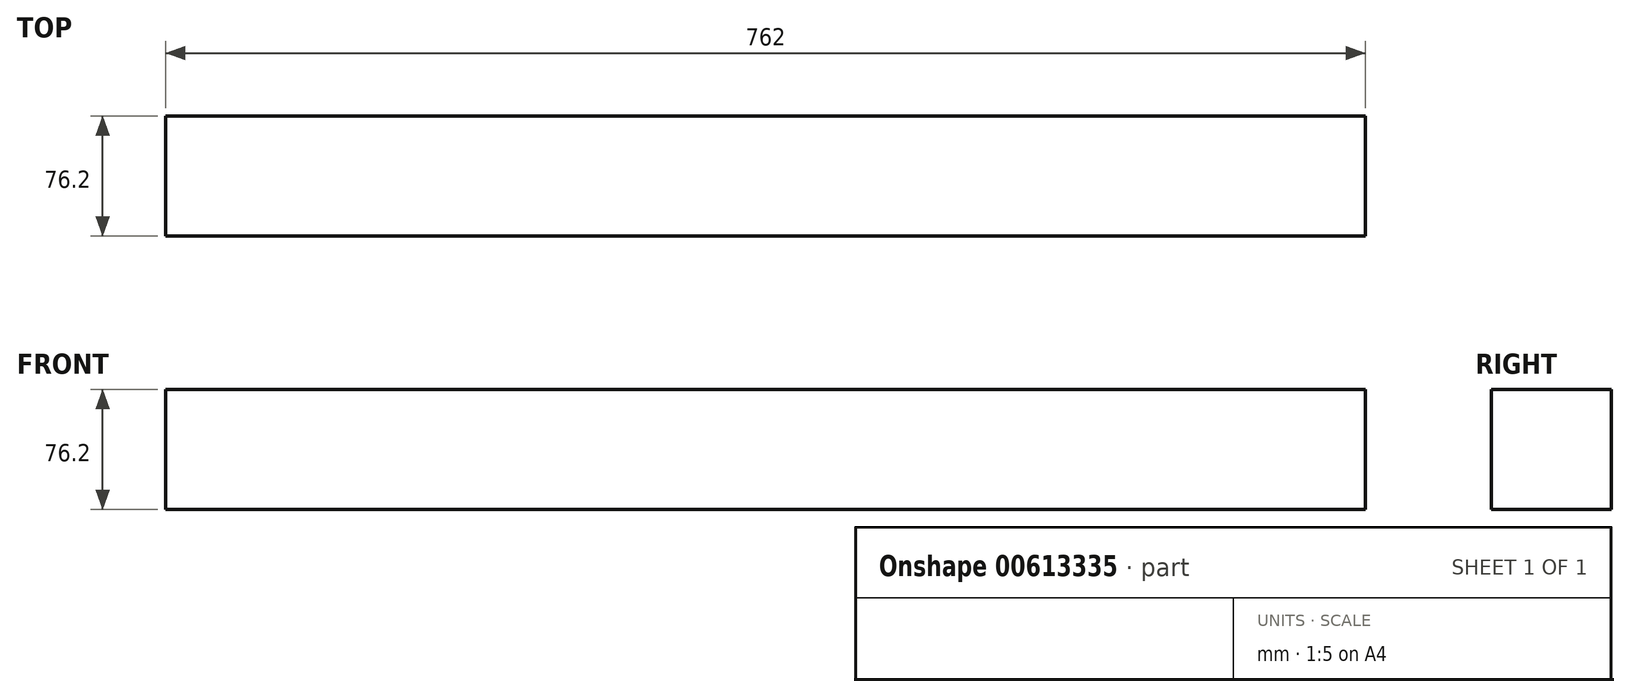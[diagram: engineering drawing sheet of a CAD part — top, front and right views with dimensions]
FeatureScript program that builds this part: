
annotation { "Feature Type Name" : "Feature", "Feature Type Description" : "" }
export const myFeature = defineFeature(function(context is Context, id is Id, definition is map)
    precondition{}
    {
        {
            var Q0;
            Q0=qCreatedBy(makeId("Right.planeOp"),FACE);
            var sketch = newSketch(context, id + "F0", { "sketchPlane" : qUnion([Q0])});
            skLineSegment(sketch, "E0.bottom", {"start": v(38.1, 38.1) * mm, "end": v(-38.1, 38.1) * mm});
            skLineSegment(sketch, "E0.top", {"start": v(38.1, -38.1) * mm, "end": v(-38.1, -38.1) * mm});
            skLineSegment(sketch, "E0.left", {"start": v(38.1, 38.1) * mm, "end": v(38.1, -38.1) * mm});
            skLineSegment(sketch, "E0.right", {"start": v(-38.1, 38.1) * mm, "end": v(-38.1, -38.1) * mm});
            skPoint(sketch, "E0.middle", {"position": v(0, 0) * mm});
            skSolve(sketch);
        }
        {
            var Q0;
            Q0 = qSketchRegion(id + "F0", true);
            extrude(context, id + "F1", {"entities" : qUnion([Q0]), "depth" : 762 * mm, "offsetDistance" : 25.4 * mm});
        }
    });
